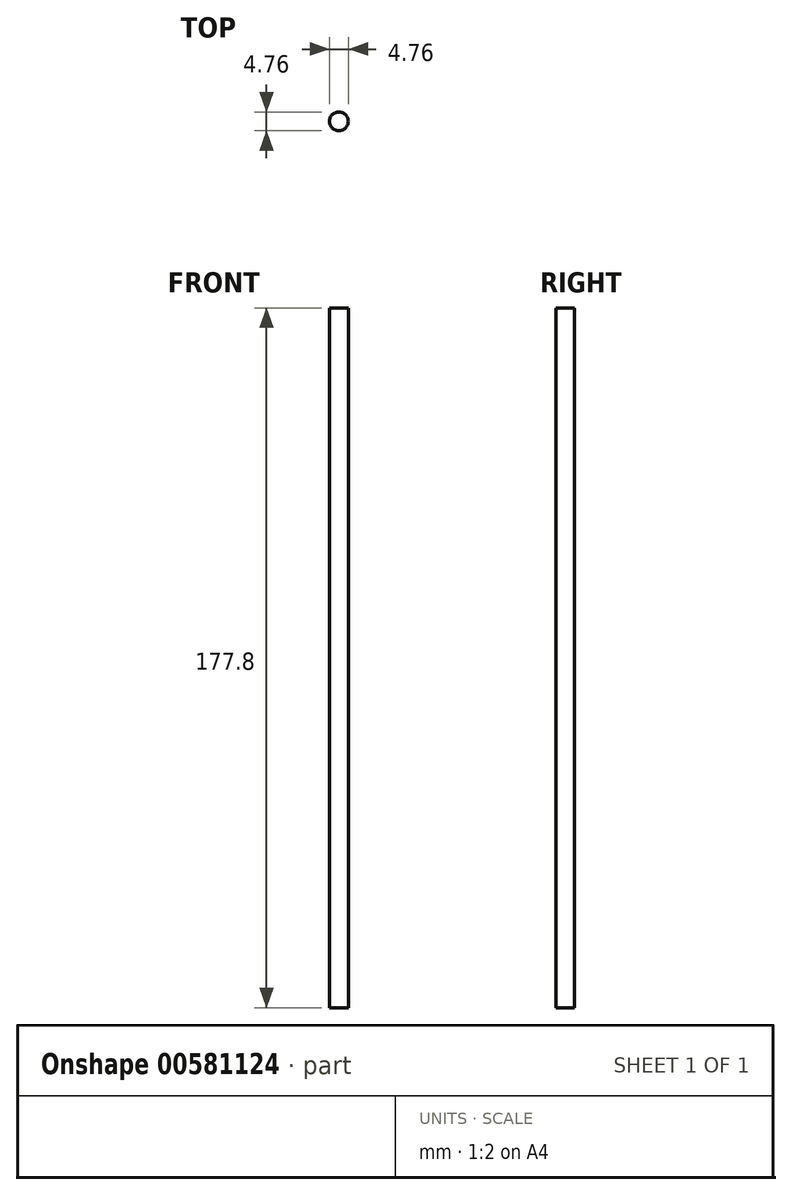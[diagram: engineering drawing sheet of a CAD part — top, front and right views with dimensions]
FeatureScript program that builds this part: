
annotation { "Feature Type Name" : "Feature", "Feature Type Description" : "" }
export const myFeature = defineFeature(function(context is Context, id is Id, definition is map)
    precondition{}
    {
        {
            var Q0;
            Q0=qCreatedBy(makeId("Top.planeOp"),FACE);
            var sketch = newSketch(context, id + "F0", { "sketchPlane" : qUnion([Q0])});
            skCircle(sketch, "E0", {"center": v(0, 0) * mm, "radius": 2.38 * mm});
            skSolve(sketch);
        }
        {
            var Q0;
            Q0=makeQuery(id+"F0.imprint","IMPRINT",FACE,{"disambiguationData":[TD([[makeQuery(id+"F0.imprint","IMPRINT",EDGE,{"derivedFrom":sQuery(id+"F0.wireOp",EDGE,"E0")}),1.0]])]});
            extrude(context, id + "F1", {"entities" : qUnion([Q0]), "depth" : 177.8 * mm, "offsetDistance" : 25.4 * mm});
        }
    });
